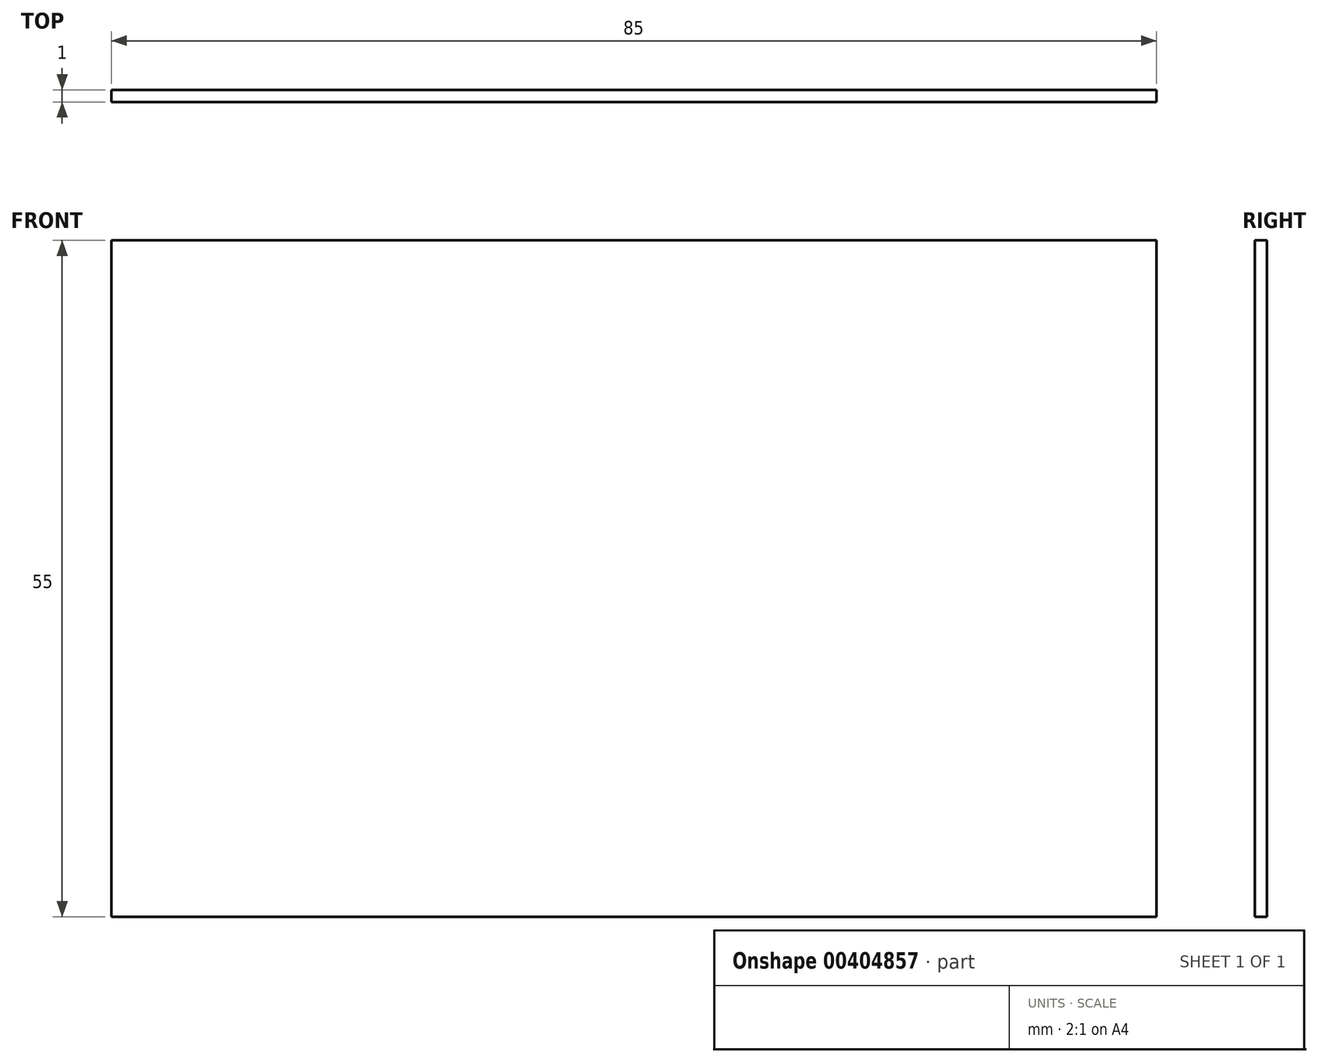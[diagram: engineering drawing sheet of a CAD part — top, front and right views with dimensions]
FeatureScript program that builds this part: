
annotation { "Feature Type Name" : "Feature", "Feature Type Description" : "" }
export const myFeature = defineFeature(function(context is Context, id is Id, definition is map)
    precondition{}
    {
        {
            var Q0;
            Q0=qCreatedBy(makeId("Front.planeOp"),FACE);
            var sketch = newSketch(context, id + "F0", { "sketchPlane" : qUnion([Q0])});
            skLineSegment(sketch, "E0.bottom", {"start": v(0, 0) * mm, "end": v(-85, 0) * mm});
            skLineSegment(sketch, "E0.top", {"start": v(0, 55) * mm, "end": v(-85, 55) * mm});
            skLineSegment(sketch, "E0.left", {"start": v(0, 0) * mm, "end": v(0, 55) * mm});
            skLineSegment(sketch, "E0.right", {"start": v(-85, 0) * mm, "end": v(-85, 55) * mm});
            skSolve(sketch);
        }
        {
            var Q0;
            Q0 = qSketchRegion(id + "F0", true);
            extrude(context, id + "F1", {"entities" : qUnion([Q0]), "depth" : 1 * mm});
        }
    });
